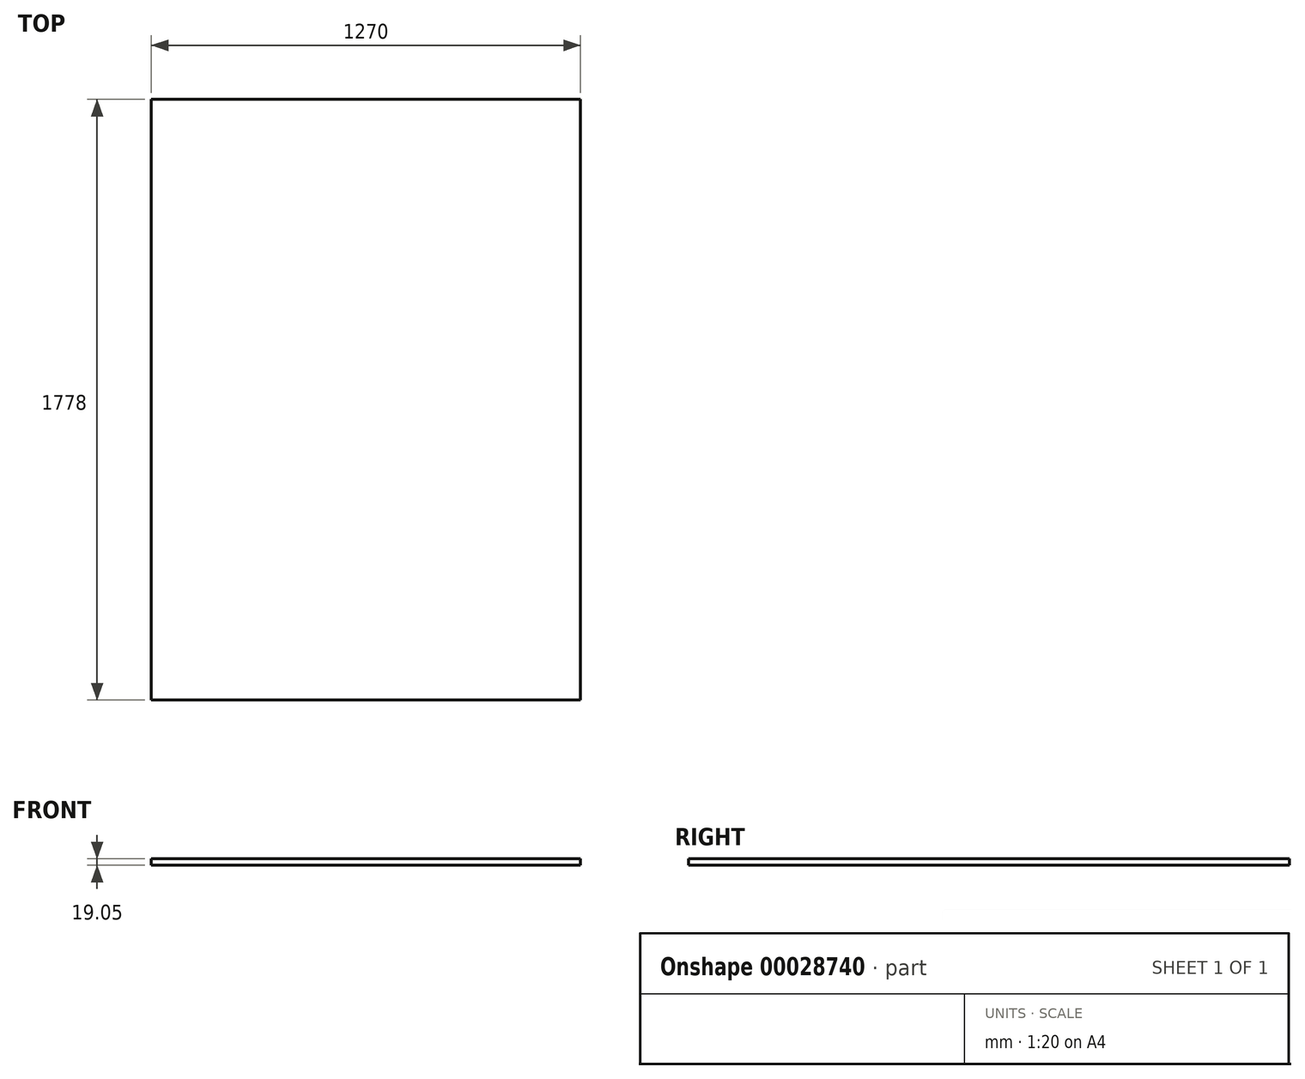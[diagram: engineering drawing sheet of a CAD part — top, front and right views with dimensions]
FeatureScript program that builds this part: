
annotation { "Feature Type Name" : "Feature", "Feature Type Description" : "" }
export const myFeature = defineFeature(function(context is Context, id is Id, definition is map)
    precondition{}
    {
        {
            var Q0;
            Q0=qCreatedBy(makeId("Top.planeOp"),FACE);
            var sketch = newSketch(context, id + "F0", { "sketchPlane" : qUnion([Q0])});
            skLineSegment(sketch, "E0.bottom", {"start": v(-982.95, 894.51) * mm, "end": v(287.05, 894.51) * mm});
            skLineSegment(sketch, "E0.top", {"start": v(-982.95, -883.49) * mm, "end": v(287.05, -883.49) * mm});
            skLineSegment(sketch, "E0.left", {"start": v(-982.95, 894.51) * mm, "end": v(-982.95, -883.49) * mm});
            skLineSegment(sketch, "E0.right", {"start": v(287.05, 894.51) * mm, "end": v(287.05, -883.49) * mm});
            skSolve(sketch);
        }
        {
            var Q0;
            Q0 = qSketchRegion(id + "F0", true);
            extrude(context, id + "F1", {"entities" : qUnion([Q0]), "depth" : 19.05 * mm});
        }
    });
